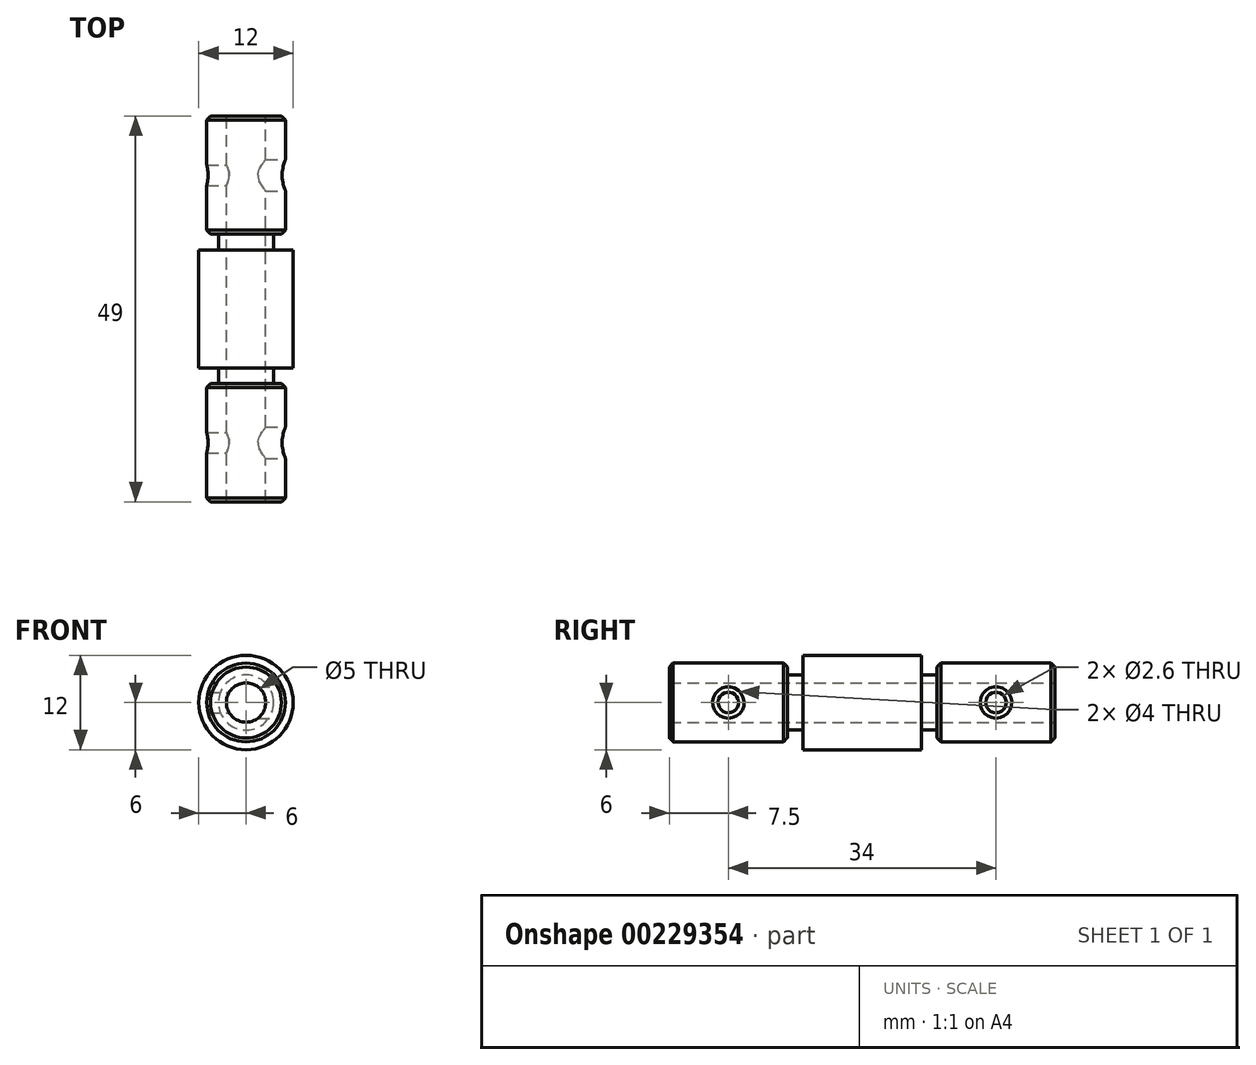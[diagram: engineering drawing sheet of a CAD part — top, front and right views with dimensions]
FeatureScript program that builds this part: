
annotation { "Feature Type Name" : "Feature", "Feature Type Description" : "" }
export const myFeature = defineFeature(function(context is Context, id is Id, definition is map)
    precondition{}
    {
        {
            var Q0;
            Q0=qCreatedBy(makeId("Front.planeOp"),FACE);
            var sketch = newSketch(context, id + "F0", { "sketchPlane" : qUnion([Q0])});
            skCircle(sketch, "E0", {"center": v(0, 0) * mm, "radius": 5 * mm});
            skSolve(sketch);
        }
        {
            var Q0;
            Q0 = qSketchRegion(id + "F0", true);
            extrude(context, id + "F1", {"entities" : qUnion([Q0]), "depth" : 15 * mm});
        }
        {
            var Q0;
            Q0=makeQuery(id+"F1.opExtrude","CAP_FACE",FACE,{"disambiguationData":[OSD([sQuery(id+"F0.wireOp",EDGE,"E0")])],"isStart":false});
            var sketch = newSketch(context, id + "F2", { "sketchPlane" : qUnion([Q0])});
            skCircle(sketch, "E1", {"center": v(0, 0) * mm, "radius": 3.5 * mm});
            skSolve(sketch);
        }
        {
            var Q0;
            Q0=makeQuery(id+"F2.imprint","IMPRINT",FACE,{"disambiguationData":[TD([[makeQuery(id+"F2.imprint","IMPRINT",EDGE,{"derivedFrom":sQuery(id+"F2.wireOp",EDGE,"E1")}),1.0]])]});
            extrude(context, id + "F3", {"entities" : qUnion([Q0]), "operationType" : NewBodyOperationType.ADD, "depth" : 2 * mm});
        }
        {
            var Q0;
            Q0=makeQuery(id+"F3.opExtrude","CAP_FACE",FACE,{"disambiguationData":[OSD([sQuery(id+"F2.wireOp",EDGE,"E1")])],"isStart":false});
            var sketch = newSketch(context, id + "F4", { "sketchPlane" : qUnion([Q0])});
            skCircle(sketch, "E2", {"center": v(0, 0) * mm, "radius": 6 * mm});
            skSolve(sketch);
        }
        {
            var Q0;
            Q0 = qSketchRegion(id + "F4", true);
            extrude(context, id + "F5", {"entities" : qUnion([Q0]), "operationType" : NewBodyOperationType.ADD, "depth" : 15 * mm});
        }
        {
            var Q0;
            Q0=makeQuery(id+"F5.opExtrude","CAP_FACE",FACE,{"disambiguationData":[OSD([sQuery(id+"F4.wireOp",EDGE,"E2")])],"isStart":false});
            var sketch = newSketch(context, id + "F6", { "sketchPlane" : qUnion([Q0])});
            skCircle(sketch, "E3", {"center": v(0, 0) * mm, "radius": 3.5 * mm});
            skSolve(sketch);
        }
        {
            var Q0;
            Q0 = qSketchRegion(id + "F6", true);
            extrude(context, id + "F7", {"entities" : qUnion([Q0]), "operationType" : NewBodyOperationType.ADD, "depth" : 2 * mm});
        }
        {
            var Q0;
            Q0=makeQuery(id+"F7.opExtrude","CAP_FACE",FACE,{"disambiguationData":[OSD([sQuery(id+"F6.wireOp",EDGE,"E3")])],"isStart":false});
            var sketch = newSketch(context, id + "F8", { "sketchPlane" : qUnion([Q0])});
            skCircle(sketch, "E4", {"center": v(0, 0) * mm, "radius": 5 * mm});
            skSolve(sketch);
        }
        {
            var Q0;
            Q0 = qSketchRegion(id + "F8", true);
            extrude(context, id + "F9", {"entities" : qUnion([Q0]), "operationType" : NewBodyOperationType.ADD, "depth" : 15 * mm});
        }
        {
            var Q0;
            Q0=makeQuery(id+"F9.opExtrude","CAP_EDGE",EDGE,{"disambiguationData":[OSD([sQuery(id+"F8.wireOp",EDGE,"E4")])],"isStart":false});
            var Q1;
            Q1=makeQuery(id+"F9.opExtrude","CAP_EDGE",EDGE,{"disambiguationData":[OSD([sQuery(id+"F8.wireOp",EDGE,"E4")])],"isStart":true});
            var Q2;
            Q2=makeQuery(id+"F1.opExtrude","CAP_EDGE",EDGE,{"disambiguationData":[OSD([sQuery(id+"F0.wireOp",EDGE,"E0")])],"isStart":true});
            var Q3;
            Q3=makeQuery(id+"F1.opExtrude","CAP_EDGE",EDGE,{"disambiguationData":[OSD([sQuery(id+"F0.wireOp",EDGE,"E0")])],"isStart":false});
            chamfer(context, id + "F10", {"entities" : qUnion([Q0, Q1, Q2, Q3]), "width" : .5 * mm, "tangentPropagation" : true});
        }
        {
            var Q0;
            Q0=qCreatedBy(makeId("Right.planeOp"),FACE);
            cPlane(context, id + "F11", {"entities" : qUnion([Q0]), "cplaneType" : CPlaneType.OFFSET, "offset" : 5 * mm, "width" : 150 * mm, "height" : 150 * mm});
        }
        {
            var Q0;
            Q0=qCreatedBy(id+"F11.planeOp",FACE);
            var sketch = newSketch(context, id + "F12", { "sketchPlane" : qUnion([Q0])});
            skLineSegment(sketch, "E5", {"start": v(0, 0) * mm, "end": v(-7.5, 0) * mm, "construction": true});
            skLineSegment(sketch, "E6", {"start": v(-7.5, 0) * mm, "end": v(-41.5, 0) * mm, "construction": true});
            skCircle(sketch, "E7", {"center": v(-41.5, 0) * mm, "radius": 1.3 * mm});
            skCircle(sketch, "E8", {"center": v(-7.5, 0) * mm, "radius": 1.3 * mm});
            skCircle(sketch, "E9", {"center": v(-41.5, 0) * mm, "radius": 2 * mm});
            skCircle(sketch, "E10", {"center": v(-7.5, 0) * mm, "radius": 2 * mm});
            skSolve(sketch);
        }
        {
            var Q0;
            Q0=makeQuery(id+"F12.imprint","IMPRINT",FACE,{"disambiguationData":[TD([[makeQuery(id+"F12.imprint","IMPRINT",EDGE,{"derivedFrom":sQuery(id+"F12.wireOp",EDGE,"E8")}),1.0]])]});
            var Q1;
            Q1=makeQuery(id+"F12.imprint","IMPRINT",FACE,{"disambiguationData":[TD([[makeQuery(id+"F12.imprint","IMPRINT",EDGE,{"derivedFrom":sQuery(id+"F12.wireOp",EDGE,"E7")}),1.0]])]});
            extrude(context, id + "F13", {"entities" : qUnion([Q0, Q1]), "operationType" : NewBodyOperationType.REMOVE, "oppositeDirection" : true, "depth" : 25 * mm});
        }
        {
            var Q0;
            Q0=makeQuery(id+"F12.imprint","IMPRINT",FACE,{"disambiguationData":[TD([[makeQuery(id+"F12.imprint","IMPRINT",EDGE,{"derivedFrom":sQuery(id+"F12.wireOp",EDGE,"E7")}),-1.0]])]});
            var Q1;
            Q1=makeQuery(id+"F12.imprint","IMPRINT",FACE,{"disambiguationData":[TD([[makeQuery(id+"F12.imprint","IMPRINT",EDGE,{"derivedFrom":sQuery(id+"F12.wireOp",EDGE,"E8")}),-1.0]])]});
            extrude(context, id + "F14", {"entities" : qUnion([Q0, Q1]), "operationType" : NewBodyOperationType.REMOVE, "oppositeDirection" : true, "depth" : 5 * mm});
        }
        {
            var Q0;
            Q0=makeQuery(id+"F1.opExtrude","CAP_FACE",FACE,{"disambiguationData":[OSD([sQuery(id+"F0.wireOp",EDGE,"E0")])],"isStart":true});
            var sketch = newSketch(context, id + "F15", { "sketchPlane" : qUnion([Q0])});
            skCircle(sketch, "E11", {"center": v(0, 0) * mm, "radius": 2.5 * mm});
            skSolve(sketch);
        }
        {
            var Q0;
            Q0 = qSketchRegion(id + "F15", true);
            extrude(context, id + "F16", {"entities" : qUnion([Q0]), "operationType" : NewBodyOperationType.REMOVE, "oppositeDirection" : true, "depth" : 50 * mm});
        }
    });
